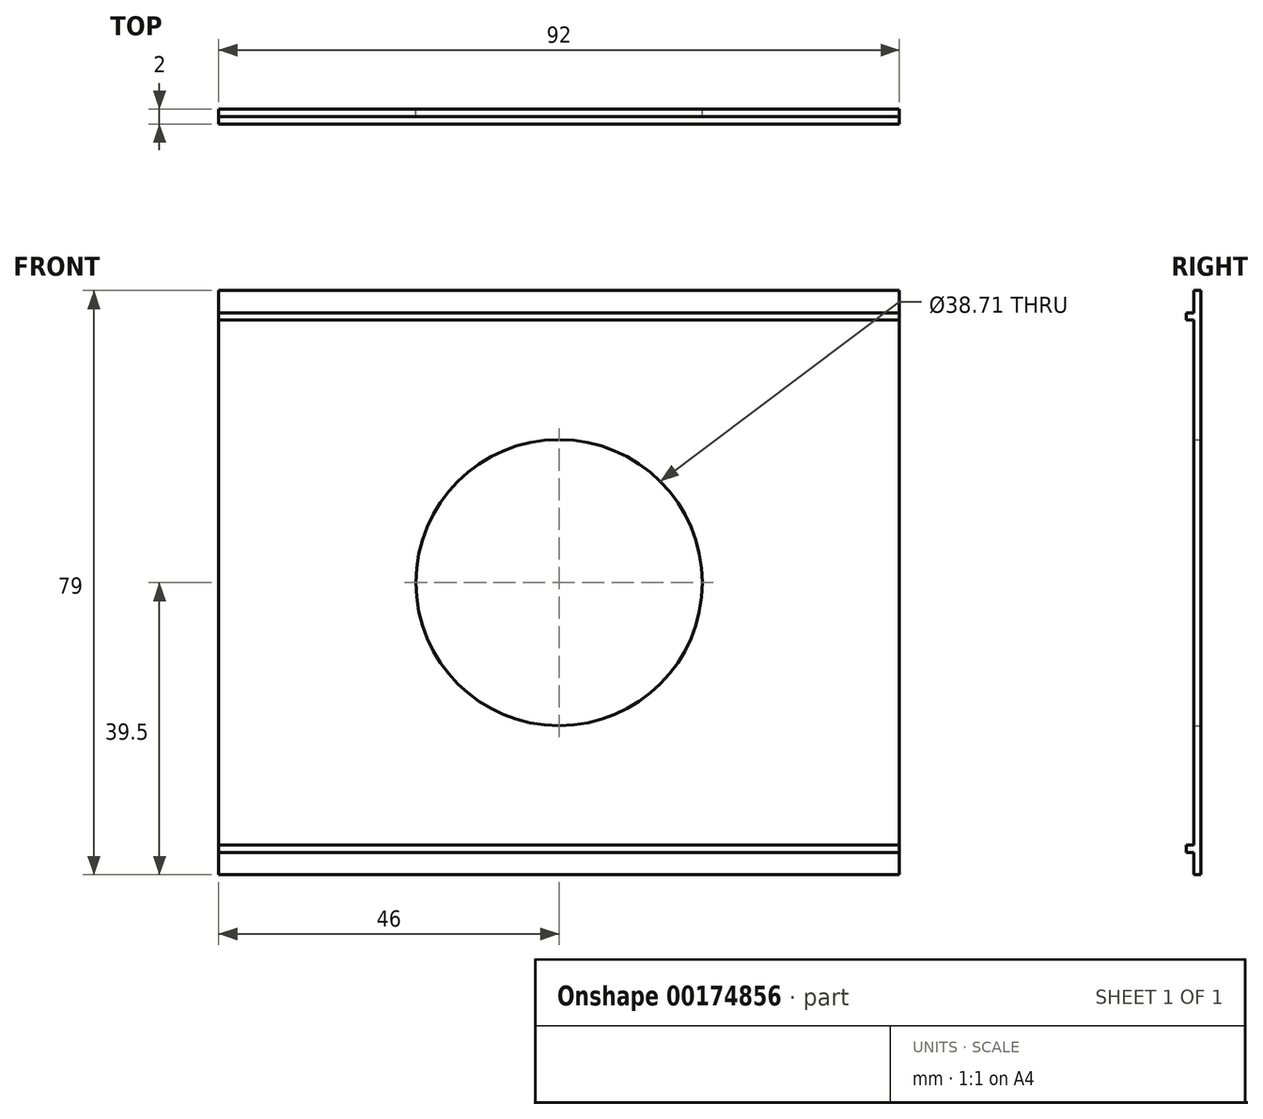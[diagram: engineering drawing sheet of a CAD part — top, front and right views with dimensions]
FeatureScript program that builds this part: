
annotation { "Feature Type Name" : "Feature", "Feature Type Description" : "" }
export const myFeature = defineFeature(function(context is Context, id is Id, definition is map)
    precondition{}
    {
        {
            var Q0;
            Q0=qCreatedBy(makeId("Front.planeOp"),FACE);
            var sketch = newSketch(context, id + "F0", { "sketchPlane" : qUnion([Q0])});
            skLineSegment(sketch, "E0.bottom", {"start": v(46, 39.5) * mm, "end": v(-46, 39.5) * mm});
            skLineSegment(sketch, "E0.top", {"start": v(46, -39.5) * mm, "end": v(-46, -39.5) * mm});
            skLineSegment(sketch, "E0.left", {"start": v(46, 39.5) * mm, "end": v(46, -39.5) * mm});
            skLineSegment(sketch, "E0.right", {"start": v(-46, 39.5) * mm, "end": v(-46, -39.5) * mm});
            skPoint(sketch, "E0.middle", {"position": v(0, 0) * mm});
            skCircle(sketch, "E1", {"center": v(0, 0) * mm, "radius": 19.35 * mm});
            skSolve(sketch);
        }
        {
            var Q0;
            Q0=makeQuery(id+"F0.imprint","IMPRINT",FACE,{"disambiguationData":[TD([[makeQuery(id+"F0.imprint","IMPRINT",EDGE,{"derivedFrom":sQuery(id+"F0.wireOp",EDGE,"E0.bottom")}),1.0]])]});
            extrude(context, id + "F1", {"entities" : qUnion([Q0]), "depth" : 1 * mm});
        }
        {
            var Q0;
            Q0=makeQuery(id+"F1.opExtrude","CAP_FACE",FACE,{"disambiguationData":[OSD([sQuery(id+"F0.wireOp",EDGE,"E0.bottom"),sQuery(id+"F0.wireOp",EDGE,"E0.top"),sQuery(id+"F0.wireOp",EDGE,"E0.left"),sQuery(id+"F0.wireOp",EDGE,"E0.right"),sQuery(id+"F0.wireOp",EDGE,"E1")])],"isStart":false});
            var sketch = newSketch(context, id + "F2", { "sketchPlane" : qUnion([Q0])});
            skLineSegment(sketch, "E2.bottom", {"start": v(46, 35.5) * mm, "end": v(-46, 35.5) * mm});
            skLineSegment(sketch, "E2.top", {"start": v(46, 36.5) * mm, "end": v(-46, 36.5) * mm});
            skLineSegment(sketch, "E2.left", {"start": v(46, 35.5) * mm, "end": v(46, 36.5) * mm});
            skLineSegment(sketch, "E2.right", {"start": v(-46, 35.5) * mm, "end": v(-46, 36.5) * mm});
            skPoint(sketch, "E2.middle", {"position": v(0, 36) * mm});
            skLineSegment(sketch, "E3.bottom", {"start": v(46, -35.5) * mm, "end": v(-46, -35.5) * mm});
            skLineSegment(sketch, "E3.top", {"start": v(46, -36.5) * mm, "end": v(-46, -36.5) * mm});
            skLineSegment(sketch, "E3.left", {"start": v(46, -35.5) * mm, "end": v(46, -36.5) * mm});
            skLineSegment(sketch, "E3.right", {"start": v(-46, -35.5) * mm, "end": v(-46, -36.5) * mm});
            skPoint(sketch, "E3.middle", {"position": v(0, -36) * mm});
            skSolve(sketch);
        }
        {
            var Q0;
            Q0 = qSketchRegion(id + "F2", true);
            extrude(context, id + "F3", {"entities" : qUnion([Q0]), "operationType" : NewBodyOperationType.ADD, "depth" : 1 * mm});
        }
    });
